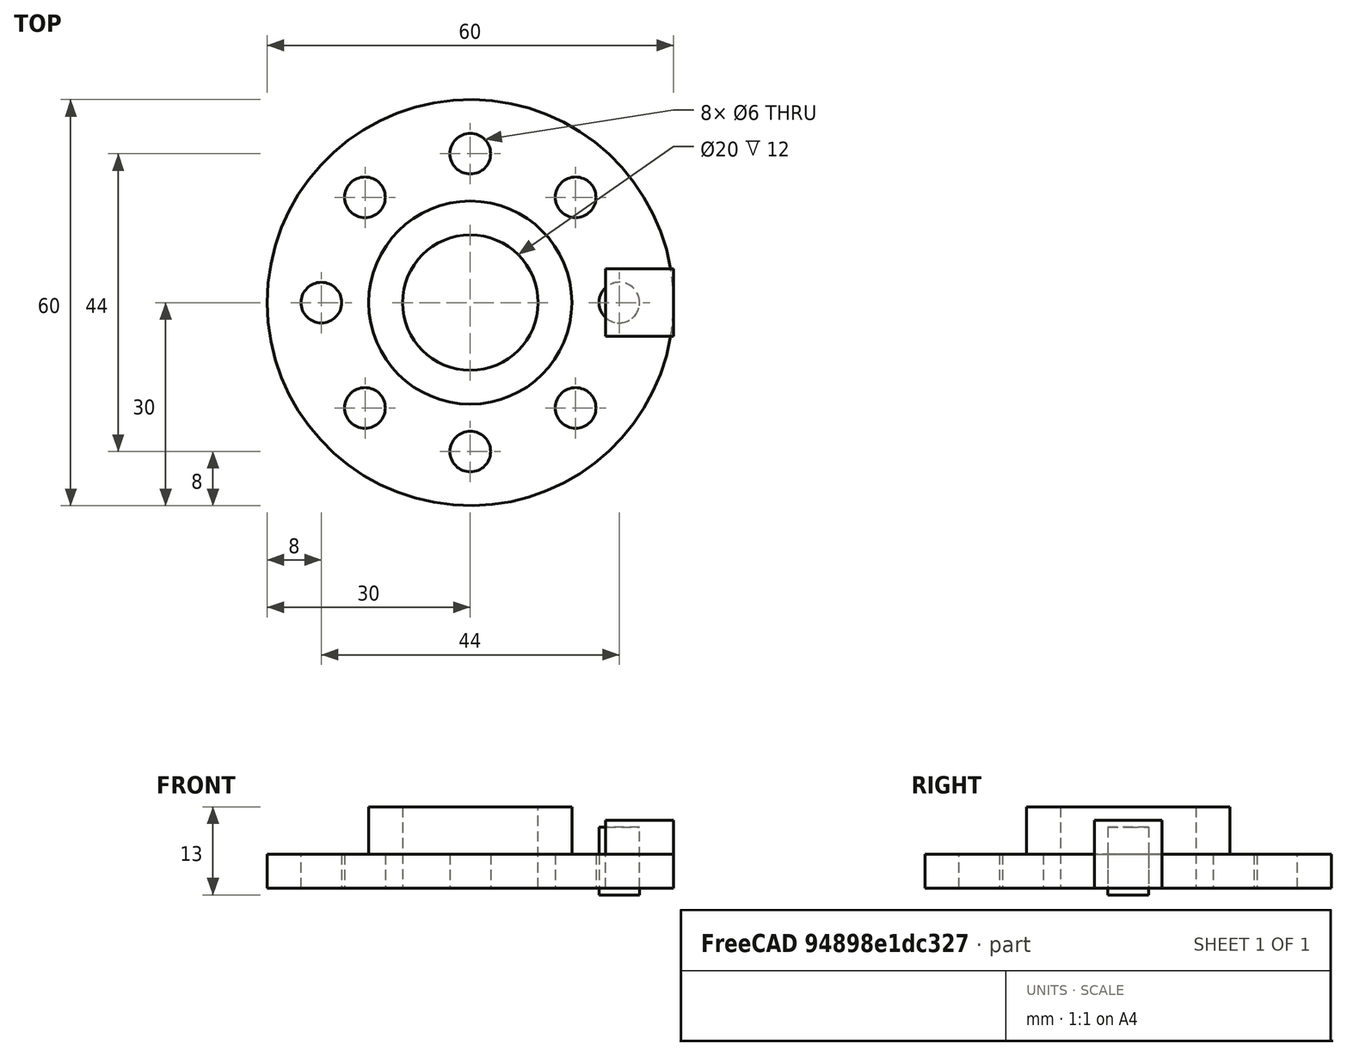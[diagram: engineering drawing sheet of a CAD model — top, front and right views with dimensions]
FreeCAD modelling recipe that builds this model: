
FCSTD DOCUMENT  (FreeCAD 0.21R33694 (Git))
Label: OJT1_T11P01_bridasensetaladres
License: All rights reserved
LicenseURL: https://en.wikipedia.org/wiki/All_rights_reserved
objects: Part::Cylinder×4, Part::FeaturePython×2, Part::Cut×2, Part::Box×1, Part::MultiFuse×1
note: 8 computed .brp shape members not serialized (recipe doc carries the construction recipe); baked Part::Feature solids carry a one-line shape summary decoded from their .brp

FEATURE [Part::Box] Box  label="Cub"
  AttacherType = Attacher::AttachEngine3D
  Height = 10
  Length = 10
  Placement = pos=(20,-5,0) rot=(0,0,1;0rad)
  Width = 10
FEATURE [Part::FeaturePython] Array  # Draft array (typed FeaturePython)
  AlwaysSyncPlacement = false
  Angle = 180
  ArrayType = 1
  Axis = (0,0,1)
  Base = -> Box
  Center = (0,0,0)
  Count = 6
  ExpandArray = false
  Fuse = false
  IntervalAxis = (0,0,0)
  IntervalX = (100,0,0)
  IntervalY = (0,100,0)
  IntervalZ = (0,0,100)
  NumberCircles = 3
  NumberPolar = 6
  NumberX = 2
  NumberY = 2
  NumberZ = 1
  PlacementList = 6 placements: [(20,-5,0),(19.1193,7.71062,0),(10.9356,17.476,0),(-1.42506,20.5662,0),(-13.2414,15.8008,0),(-20,5,0)]
  RadialDistance = 50
  ScaleList = (6) [(1,1,1),(1,1,1),(1,1,1),(1,1,1),(1,1,1),(1,1,1)]
  Symmetry = 1
  TangentialDistance = 25
FEATURE [Part::Cylinder] Cylinder  label="Base"
  Angle = 360
  AttacherType = Attacher::AttachEngine3D
  FirstAngle = 0
  Height = 5
  Radius = 30
  SecondAngle = 0
FEATURE [Part::Cylinder] Cylinder001  label="Tub_exterior"
  Angle = 360
  AttacherType = Attacher::AttachEngine3D
  FirstAngle = 0
  Height = 12
  Radius = 15
  SecondAngle = 0
FEATURE [Part::MultiFuse] Fusion
  Shapes = -> [Cylinder,Cylinder001]
FEATURE [Part::Cylinder] Cylinder002  label="Tub_Interior"
  Angle = 360
  AttacherType = Attacher::AttachEngine3D
  FirstAngle = 0
  Height = 30
  Placement = pos=(0,0,-1) rot=(0,0,1;0rad)
  Radius = 10
  SecondAngle = 0
FEATURE [Part::Cut] Cut  label="Brida sense els taladres"
  Base = -> Fusion
  Tool = -> Cylinder002
FEATURE [Part::Cylinder] Cylinder003  label="Taladre_master"
  Angle = 360
  AttacherType = Attacher::AttachEngine3D
  FirstAngle = 0
  Height = 10
  Placement = pos=(22,0,-1) rot=(0,0,1;0rad)
  Radius = 3
  SecondAngle = 0
FEATURE [Part::FeaturePython] Array001  # Draft array (typed FeaturePython)
  AlwaysSyncPlacement = false
  Angle = 360
  ArrayType = 1
  Axis = (0,0,1)
  Base = -> Cylinder003
  Center = (0,0,0)
  Count = 8
  ExpandArray = false
  Fuse = false
  IntervalAxis = (0,0,0)
  IntervalX = (100,0,0)
  IntervalY = (0,100,0)
  IntervalZ = (0,0,100)
  NumberCircles = 3
  NumberPolar = 8
  NumberX = 2
  NumberY = 2
  NumberZ = 1
  PlacementList = 8 placements: [(22,0,-1),(15.5563,15.5563,-1),(0,22,-1),(-15.5563,15.5563,-1),(-22,2.69422e-15,-1),(-15.5563,-15.5563,-1),(-4.88498e-15,-22,-1),(15.5563,-15.5563,-1)]
  RadialDistance = 50
  ScaleList = (8) [(1,1,1),(1,1,1),(1,1,1),(1,1,1),(1,1,1),(1,1,1),(1,1,1),(1,1,1)]
  Symmetry = 1
  TangentialDistance = 25
FEATURE [Part::Cut] Cut001
  Base = -> Cut
  Tool = -> Array001
